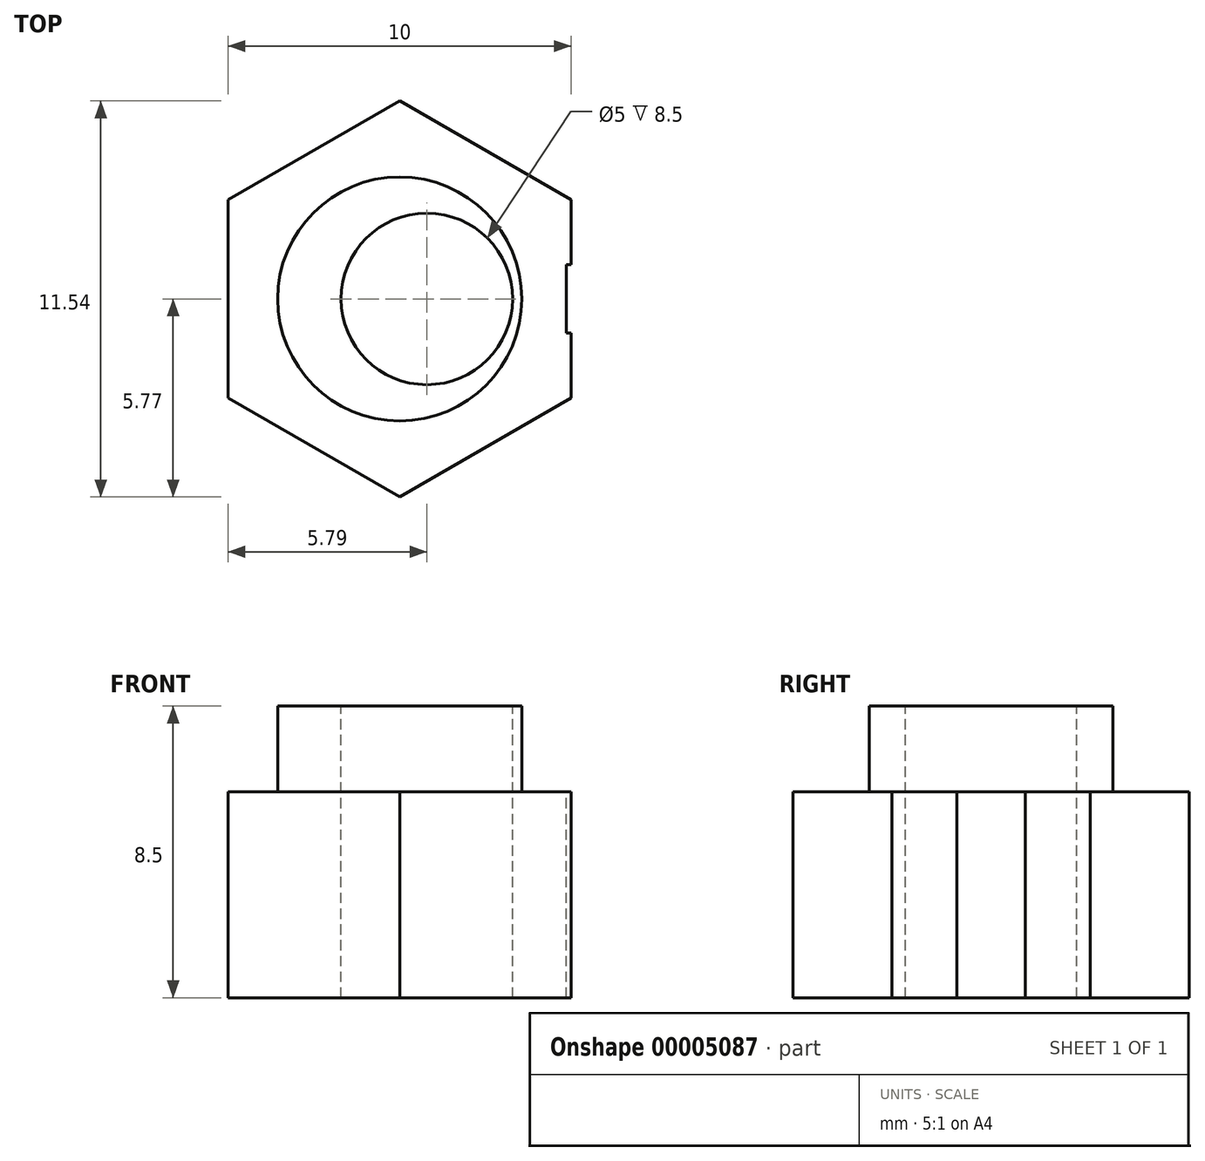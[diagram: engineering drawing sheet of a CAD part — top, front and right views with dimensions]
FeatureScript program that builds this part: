
annotation { "Feature Type Name" : "Feature", "Feature Type Description" : "" }
export const myFeature = defineFeature(function(context is Context, id is Id, definition is map)
    precondition{}
    {
        {
            var Q0;
            Q0=qCreatedBy(makeId("Top.planeOp"),FACE);
            var sketch = newSketch(context, id + "F0", { "sketchPlane" : qUnion([Q0])});
            skCircle(sketch, "E0.cCircle", {"center": v(0, 0) * mm, "radius": 5 * mm, "construction": true});
            skLineSegment(sketch, "E0.0", {"start": v(5, 2.89) * mm, "end": v(5, -2.89) * mm});
            skLineSegment(sketch, "E0.1", {"start": v(5, -2.89) * mm, "end": v(0, -5.77) * mm});
            skLineSegment(sketch, "E0.2", {"start": v(0, -5.77) * mm, "end": v(-5, -2.89) * mm});
            skLineSegment(sketch, "E0.3", {"start": v(-5, -2.89) * mm, "end": v(-5, 2.89) * mm});
            skLineSegment(sketch, "E0.4", {"start": v(-5, 2.89) * mm, "end": v(0, 5.77) * mm});
            skLineSegment(sketch, "E0.5", {"start": v(0, 5.77) * mm, "end": v(5, 2.89) * mm});
            skPoint(sketch, "E0.0.midPoint", {"position": v(5, 0) * mm});
            skSolve(sketch);
        }
        {
            var Q0;
            Q0=makeQuery(id+"F0.imprint","IMPRINT",FACE,{"disambiguationData":[TD([[makeQuery(id+"F0.imprint","IMPRINT",EDGE,{"derivedFrom":sQuery(id+"F0.wireOp",EDGE,"E0.0")}),-1.0]])]});
            extrude(context, id + "F1", {"entities" : qUnion([Q0]), "depth" : 6 * mm});
        }
        {
            var Q0;
            Q0=makeQuery(id+"F1.opExtrude","CAP_FACE",FACE,{"disambiguationData":[OSD([sQuery(id+"F0.wireOp",EDGE,"E0.0"),sQuery(id+"F0.wireOp",EDGE,"E0.1"),sQuery(id+"F0.wireOp",EDGE,"E0.2"),sQuery(id+"F0.wireOp",EDGE,"E0.3"),sQuery(id+"F0.wireOp",EDGE,"E0.4"),sQuery(id+"F0.wireOp",EDGE,"E0.5")])],"isStart":false});
            var sketch = newSketch(context, id + "F2", { "sketchPlane" : qUnion([Q0])});
            skCircle(sketch, "E1", {"center": v(0, 0) * mm, "radius": 3.56 * mm});
            skSolve(sketch);
        }
        {
            var Q0;
            Q0=makeQuery(id+"F2.imprint","IMPRINT",FACE,{"disambiguationData":[TD([[makeQuery(id+"F2.imprint","IMPRINT",EDGE,{"derivedFrom":sQuery(id+"F2.wireOp",EDGE,"E1")}),1.0]])]});
            extrude(context, id + "F3", {"entities" : qUnion([Q0]), "operationType" : NewBodyOperationType.ADD, "depth" : 2.5 * mm});
        }
        {
            var Q0;
            Q0=makeQuery(id+"F3.opExtrude","CAP_FACE",FACE,{"disambiguationData":[OSD([sQuery(id+"F2.wireOp",EDGE,"E1")])],"isStart":false});
            var sketch = newSketch(context, id + "F4", { "sketchPlane" : qUnion([Q0])});
            skCircle(sketch, "E2", {"center": v(0.79, 0) * mm, "radius": 2.5 * mm});
            skSolve(sketch);
        }
        {
            var Q0;
            Q0=makeQuery(id+"F4.imprint","IMPRINT",FACE,{"disambiguationData":[TD([[makeQuery(id+"F4.imprint","IMPRINT",EDGE,{"derivedFrom":sQuery(id+"F4.wireOp",EDGE,"E2")}),1.0]])]});
            extrude(context, id + "F5", {"entities" : qUnion([Q0]), "operationType" : NewBodyOperationType.REMOVE, "endBound" : BoundingType.UP_TO_NEXT, "oppositeDirection" : true, "depth" : 25 * mm});
        }
        {
            var Q0;
            Q0=makeQuery(id+"F1.opExtrude","SWEPT_FACE",FACE,{"disambiguationData":[OSD([sQuery(id+"F0.wireOp",EDGE,"E0.0")])]});
            var sketch = newSketch(context, id + "F6", { "sketchPlane" : qUnion([Q0])});
            skLineSegment(sketch, "E3.bottom", {"start": v(-1, 0) * mm, "end": v(1, 0) * mm});
            skLineSegment(sketch, "E3.top", {"start": v(-1, 6) * mm, "end": v(1, 6) * mm});
            skLineSegment(sketch, "E3.left", {"start": v(-1, 0) * mm, "end": v(-1, 6) * mm});
            skLineSegment(sketch, "E3.right", {"start": v(1, 0) * mm, "end": v(1, 6) * mm});
            skSolve(sketch);
        }
        {
            var Q0;
            Q0=makeQuery(id+"F6.imprint","IMPRINT",FACE,{"disambiguationData":[TD([[makeQuery(id+"F6.imprint","IMPRINT",EDGE,{"derivedFrom":sQuery(id+"F6.wireOp",EDGE,"E3.bottom")}),-1.0]])]});
            extrude(context, id + "F7", {"entities" : qUnion([Q0]), "operationType" : NewBodyOperationType.REMOVE, "oppositeDirection" : true, "depth" : 0.15 * mm});
        }
    });
